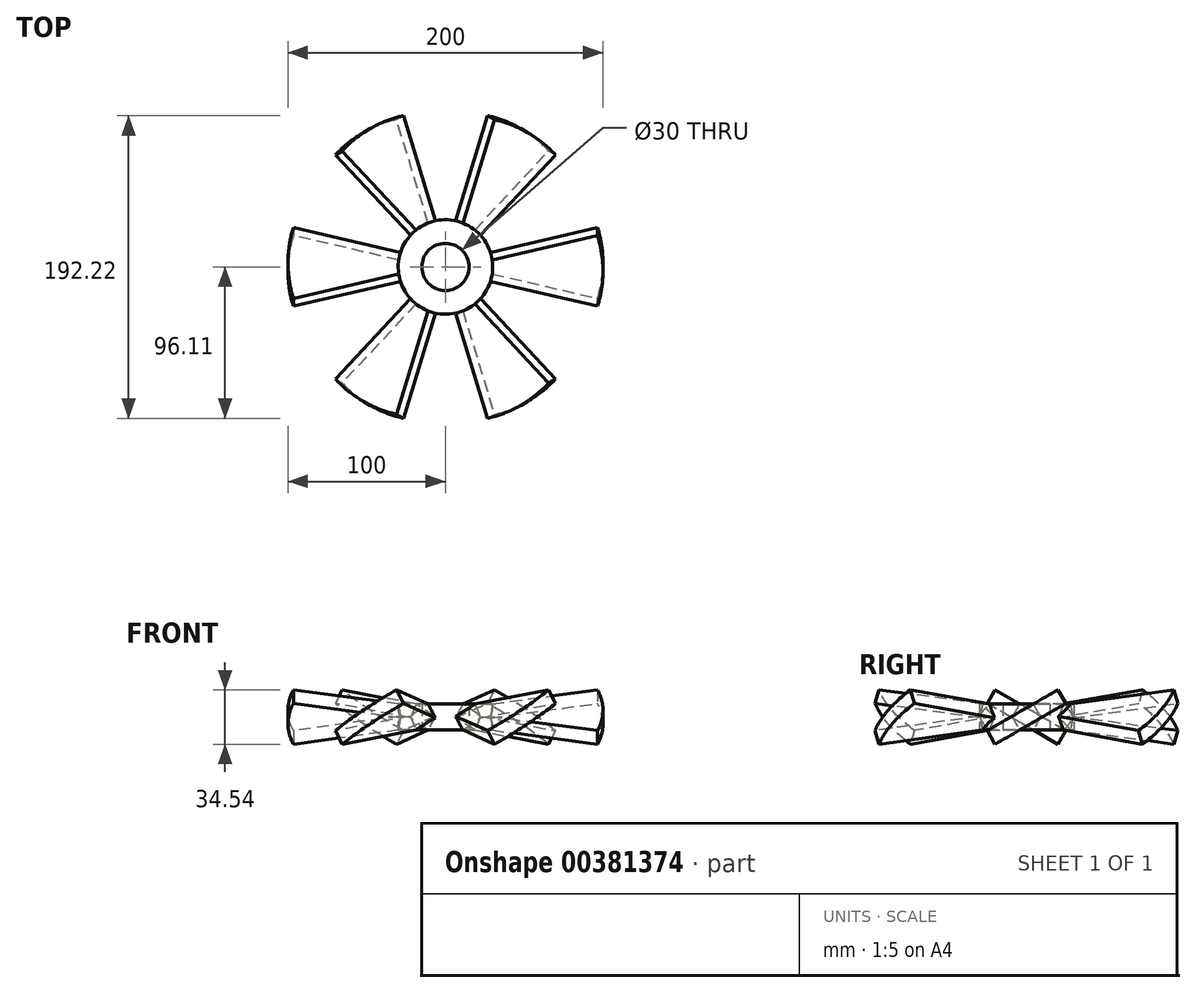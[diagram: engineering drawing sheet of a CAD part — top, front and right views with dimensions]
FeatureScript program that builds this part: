
annotation { "Feature Type Name" : "Feature", "Feature Type Description" : "" }
export const myFeature = defineFeature(function(context is Context, id is Id, definition is map)
    precondition{}
    {
        {
            var Q0;
            Q0=qCreatedBy(makeId("Top.planeOp"),FACE);
            var sketch = newSketch(context, id + "F0", { "sketchPlane" : qUnion([Q0])});
            skLineSegment(sketch, "E0", {"start": v(0, 0) * mm, "end": v(96.6, -25.88) * mm});
            skArc(sketch, "E1", {"start": v(96.6, -25.88) * mm, "mid": v(100, 0) * mm, "end": v(96.6, 25.88) * mm});
            skLineSegment(sketch, "E2", {"start": v(0, 0) * mm, "end": v(125.13, 0) * mm, "construction": true});
            skPoint(sketch, "E2.endSnap0", {"position": v(100, 0) * mm});
            skLineSegment(sketch, "E3.MirrorCS", {"start": v(0, 0) * mm, "end": v(96.6, 25.88) * mm});
            skSolve(sketch);
        }
        {
            var Q0;
            Q0=makeQuery(id+"F0.imprint","IMPRINT",FACE,{"disambiguationData":[TD([[makeQuery(id+"F0.imprint","IMPRINT",EDGE,{"derivedFrom":sQuery(id+"F0.wireOp",EDGE,"E0")}),1.0]])]});
            extrude(context, id + "F1", {"entities" : qUnion([Q0]), "depth" : 5 * mm, "hasSecondDirection" : true, "secondDirectionOppositeDirection" : true, "secondDirectionDepth" : 5 * mm});
        }
        {
            var Q0;
            Q0=qCreatedBy(makeId("Top.planeOp"),FACE);
            var sketch = newSketch(context, id + "F2", { "sketchPlane" : qUnion([Q0])});
            skLineSegment(sketch, "E4", {"start": v(0, 0) * mm, "end": v(131.6, 0) * mm, "construction": true});
            skSolve(sketch);
        }
        {
            var Q0;
            Q0=makeQuery(id+"F1.opExtrude","SWEPT_BODY",BODY,{"disambiguationData":[OSD([sQuery(id+"F0.wireOp",EDGE,"E0"),sQuery(id+"F0.wireOp",EDGE,"E1"),sQuery(id+"F0.wireOp",EDGE,"E3.MirrorCS")])]});
            var Q1;
            Q1=sQuery(id+"F2.wireOp",EDGE,"E4");
            transform(context, id + "F3", {"entities" : qUnion([Q0]), "transformType" : TransformType.ROTATION, "transformAxis" : qUnion([Q1]), "angle" : 30 * degree, "makeCopy" : false});
        }
        {
            var Q0;
            Q0=qCreatedBy(makeId("Right.planeOp"),FACE);
            var sketch = newSketch(context, id + "F4", { "sketchPlane" : qUnion([Q0])});
            skLineSegment(sketch, "E5", {"start": v(0, 0) * mm, "end": v(0, 57.62) * mm, "construction": true});
            skSolve(sketch);
        }
        {
            var Q0;
            Q0=makeQuery(id+"F1.opExtrude","SWEPT_BODY",BODY,{"disambiguationData":[OSD([sQuery(id+"F0.wireOp",EDGE,"E0"),sQuery(id+"F0.wireOp",EDGE,"E1"),sQuery(id+"F0.wireOp",EDGE,"E3.MirrorCS")])]});
            var Q1;
            Q1=sQuery(id+"F4.wireOp",EDGE,"E5");
            circularPattern(context, id + "F5", {"entities" : qUnion([Q0]), "axis" : qUnion([Q1]), "angle" : 360 * degree, "instanceCount" : 6, "equalSpace" : true});
        }
        {
            var Q0;
            Q0=qCreatedBy(makeId("Top.planeOp"),FACE);
            var sketch = newSketch(context, id + "F6", { "sketchPlane" : qUnion([Q0])});
            skCircle(sketch, "E6", {"center": v(0, 0) * mm, "radius": 30 * mm});
            skSolve(sketch);
        }
        {
            var Q0;
            Q0=makeQuery(id+"F6.imprint","IMPRINT",FACE,{"disambiguationData":[TD([[makeQuery(id+"F6.imprint","IMPRINT",EDGE,{"derivedFrom":sQuery(id+"F6.wireOp",EDGE,"E6")}),1.0]])]});
            var Q1;
            Q1=sQuery(id+"F6.wireOp",EDGE,"E6");
            extrude(context, id + "F7", {"entities" : qUnion([Q0]), "surfaceEntities" : qUnion([Q1]), "depth" : 25 * mm, "hasSecondDirection" : true, "secondDirectionOppositeDirection" : true, "secondDirectionDepth" : 25 * mm});
        }
        {
            var Q0;
            Q0=makeQuery(id+"F5.opPattern","COPY",BODY,{"derivedFrom":makeQuery(id+"F1.opExtrude","SWEPT_BODY",BODY,{"disambiguationData":[OSD([sQuery(id+"F0.wireOp",EDGE,"E0"),sQuery(id+"F0.wireOp",EDGE,"E1"),sQuery(id+"F0.wireOp",EDGE,"E3.MirrorCS")])]}),"instanceName":"3"});
            var Q1;
            Q1=makeQuery(id+"F5.opPattern","COPY",BODY,{"derivedFrom":makeQuery(id+"F1.opExtrude","SWEPT_BODY",BODY,{"disambiguationData":[OSD([sQuery(id+"F0.wireOp",EDGE,"E0"),sQuery(id+"F0.wireOp",EDGE,"E1"),sQuery(id+"F0.wireOp",EDGE,"E3.MirrorCS")])]}),"instanceName":"4"});
            var Q2;
            Q2=makeQuery(id+"F1.opExtrude","SWEPT_BODY",BODY,{"disambiguationData":[OSD([sQuery(id+"F0.wireOp",EDGE,"E0"),sQuery(id+"F0.wireOp",EDGE,"E1"),sQuery(id+"F0.wireOp",EDGE,"E3.MirrorCS")])]});
            var Q3;
            Q3=makeQuery(id+"F5.opPattern","COPY",BODY,{"derivedFrom":makeQuery(id+"F1.opExtrude","SWEPT_BODY",BODY,{"disambiguationData":[OSD([sQuery(id+"F0.wireOp",EDGE,"E0"),sQuery(id+"F0.wireOp",EDGE,"E1"),sQuery(id+"F0.wireOp",EDGE,"E3.MirrorCS")])]}),"instanceName":"1"});
            var Q4;
            Q4=makeQuery(id+"F5.opPattern","COPY",BODY,{"derivedFrom":makeQuery(id+"F1.opExtrude","SWEPT_BODY",BODY,{"disambiguationData":[OSD([sQuery(id+"F0.wireOp",EDGE,"E0"),sQuery(id+"F0.wireOp",EDGE,"E1"),sQuery(id+"F0.wireOp",EDGE,"E3.MirrorCS")])]}),"instanceName":"2"});
            var Q5;
            Q5=makeQuery(id+"F5.opPattern","COPY",BODY,{"derivedFrom":makeQuery(id+"F1.opExtrude","SWEPT_BODY",BODY,{"disambiguationData":[OSD([sQuery(id+"F0.wireOp",EDGE,"E0"),sQuery(id+"F0.wireOp",EDGE,"E1"),sQuery(id+"F0.wireOp",EDGE,"E3.MirrorCS")])]}),"instanceName":"5"});
            var Q6;
            Q6=makeQuery(id+"F7.opExtrude","SWEPT_BODY",BODY,{"disambiguationData":[OSD([sQuery(id+"F6.wireOp",EDGE,"E6")])]});
            booleanBodies(context, id + "F8", {"operationType" : BooleanOperationType.UNION, "tools" : qUnion([Q0, Q1, Q2, Q3, Q4, Q5, Q6])});
        }
        {
            var Q0;
            {var subQ0=sQuery(id+"F0.wireOp",EDGE,"E3.MirrorCS");Q0=makeQuery(id+"F8.opBoolean","INTERSECT",VERTEX,{"derivedFrom":[makeQuery(id+"F5.opPattern","COPY",FACE,{"derivedFrom":makeQuery(id+"F1.opExtrude","CAP_FACE",FACE,{"disambiguationData":[OSD([sQuery(id+"F0.wireOp",EDGE,"E0"),sQuery(id+"F0.wireOp",EDGE,"E1"),subQ0])],"isStart":false}),"instanceName":"4"}),makeQuery(id+"F5.opPattern","COPY",FACE,{"derivedFrom":makeQuery(id+"F1.opExtrude","SWEPT_FACE",FACE,{"disambiguationData":[OSD([subQ0])]}),"instanceName":"4"}),makeQuery(id+"F7.opExtrude","SWEPT_FACE",FACE,{"disambiguationData":[OSD([sQuery(id+"F6.wireOp",EDGE,"E6")])]})]});}
            var Q1;
            {var subQ0=sQuery(id+"F0.wireOp",EDGE,"E3.MirrorCS");Q1=makeQuery(id+"F8.opBoolean","INTERSECT",VERTEX,{"derivedFrom":[makeQuery(id+"F1.opExtrude","CAP_FACE",FACE,{"disambiguationData":[OSD([sQuery(id+"F0.wireOp",EDGE,"E0"),sQuery(id+"F0.wireOp",EDGE,"E1"),subQ0])],"isStart":false}),makeQuery(id+"F1.opExtrude","SWEPT_FACE",FACE,{"disambiguationData":[OSD([subQ0])]}),makeQuery(id+"F7.opExtrude","SWEPT_FACE",FACE,{"disambiguationData":[OSD([sQuery(id+"F6.wireOp",EDGE,"E6")])]})]});}
            var Q2;
            {var subQ0=sQuery(id+"F0.wireOp",EDGE,"E3.MirrorCS");Q2=makeQuery(id+"F8.opBoolean","INTERSECT",VERTEX,{"derivedFrom":[makeQuery(id+"F5.opPattern","COPY",FACE,{"derivedFrom":makeQuery(id+"F1.opExtrude","CAP_FACE",FACE,{"disambiguationData":[OSD([sQuery(id+"F0.wireOp",EDGE,"E0"),sQuery(id+"F0.wireOp",EDGE,"E1"),subQ0])],"isStart":false}),"instanceName":"2"}),makeQuery(id+"F5.opPattern","COPY",FACE,{"derivedFrom":makeQuery(id+"F1.opExtrude","SWEPT_FACE",FACE,{"disambiguationData":[OSD([subQ0])]}),"instanceName":"2"}),makeQuery(id+"F7.opExtrude","SWEPT_FACE",FACE,{"disambiguationData":[OSD([sQuery(id+"F6.wireOp",EDGE,"E6")])]})]});}
            cPlane(context, id + "F9", {"entities" : qUnion([Q0, Q1, Q2]), "cplaneType" : CPlaneType.THREE_POINT, "offset" : 25 * mm, "width" : 150 * mm, "height" : 150 * mm});
        }
        {
            var Q0;
            Q0=makeQuery(id+"F7.opExtrude","CAP_FACE",FACE,{"disambiguationData":[OSD([sQuery(id+"F6.wireOp",EDGE,"E6")])],"isStart":false});
            var Q1;
            Q1=qCreatedBy(id+"F9.planeOp",FACE);
            extrude(context, id + "F10", {"entities" : qUnion([Q0]), "operationType" : NewBodyOperationType.REMOVE, "endBound" : BoundingType.UP_TO_SURFACE, "oppositeDirection" : true, "endBoundEntityFace" : qUnion([Q1]), "depth" : 25 * mm});
        }
        {
            var Q0;
            {var subQ0=sQuery(id+"F0.wireOp",EDGE,"E0");Q0=makeQuery(id+"F8.opBoolean","INTERSECT",VERTEX,{"derivedFrom":[makeQuery(id+"F5.opPattern","COPY",FACE,{"derivedFrom":makeQuery(id+"F1.opExtrude","SWEPT_FACE",FACE,{"disambiguationData":[OSD([subQ0])]}),"instanceName":"2"}),makeQuery(id+"F5.opPattern","COPY",FACE,{"derivedFrom":makeQuery(id+"F1.opExtrude","CAP_FACE",FACE,{"disambiguationData":[OSD([subQ0,sQuery(id+"F0.wireOp",EDGE,"E1"),sQuery(id+"F0.wireOp",EDGE,"E3.MirrorCS")])],"isStart":true}),"instanceName":"2"}),makeQuery(id+"F7.opExtrude","SWEPT_FACE",FACE,{"disambiguationData":[OSD([sQuery(id+"F6.wireOp",EDGE,"E6")])]})]});}
            var Q1;
            {var subQ0=sQuery(id+"F0.wireOp",EDGE,"E0");Q1=makeQuery(id+"F8.opBoolean","INTERSECT",VERTEX,{"derivedFrom":[makeQuery(id+"F1.opExtrude","SWEPT_FACE",FACE,{"disambiguationData":[OSD([subQ0])]}),makeQuery(id+"F1.opExtrude","CAP_FACE",FACE,{"disambiguationData":[OSD([subQ0,sQuery(id+"F0.wireOp",EDGE,"E1"),sQuery(id+"F0.wireOp",EDGE,"E3.MirrorCS")])],"isStart":true}),makeQuery(id+"F7.opExtrude","SWEPT_FACE",FACE,{"disambiguationData":[OSD([sQuery(id+"F6.wireOp",EDGE,"E6")])]})]});}
            var Q2;
            {var subQ0=sQuery(id+"F0.wireOp",EDGE,"E0");Q2=makeQuery(id+"F8.opBoolean","INTERSECT",VERTEX,{"derivedFrom":[makeQuery(id+"F5.opPattern","COPY",FACE,{"derivedFrom":makeQuery(id+"F1.opExtrude","SWEPT_FACE",FACE,{"disambiguationData":[OSD([subQ0])]}),"instanceName":"4"}),makeQuery(id+"F5.opPattern","COPY",FACE,{"derivedFrom":makeQuery(id+"F1.opExtrude","CAP_FACE",FACE,{"disambiguationData":[OSD([subQ0,sQuery(id+"F0.wireOp",EDGE,"E1"),sQuery(id+"F0.wireOp",EDGE,"E3.MirrorCS")])],"isStart":true}),"instanceName":"4"}),makeQuery(id+"F7.opExtrude","SWEPT_FACE",FACE,{"disambiguationData":[OSD([sQuery(id+"F6.wireOp",EDGE,"E6")])]})]});}
            cPlane(context, id + "F11", {"entities" : qUnion([Q0, Q1, Q2]), "cplaneType" : CPlaneType.THREE_POINT, "offset" : 25 * mm, "width" : 150 * mm, "height" : 150 * mm});
        }
        {
            var Q0;
            Q0=makeQuery(id+"F7.opExtrude","CAP_FACE",FACE,{"disambiguationData":[OSD([sQuery(id+"F6.wireOp",EDGE,"E6")])],"isStart":true});
            var Q1;
            Q1=qCreatedBy(id+"F11.planeOp",FACE);
            extrude(context, id + "F12", {"entities" : qUnion([Q0]), "operationType" : NewBodyOperationType.REMOVE, "endBound" : BoundingType.UP_TO_SURFACE, "oppositeDirection" : true, "endBoundEntityFace" : qUnion([Q1]), "depth" : 25 * mm});
        }
        {
            var Q0;
            Q0=makeQuery(id+"F12.boolean.opBoolean","COPY",FACE,{"derivedFrom":makeQuery(id+"F12.opExtrude","CAP_FACE",FACE,{"disambiguationData":[OSD([sQuery(id+"F6.wireOp",EDGE,"E6")])],"isStart":false})});
            var sketch = newSketch(context, id + "F13", { "sketchPlane" : qUnion([Q0])});
            skCircle(sketch, "E7", {"center": v(0, 0) * mm, "radius": 15 * mm});
            skSolve(sketch);
        }
        {
            var Q0;
            Q0=makeQuery(id+"F13.imprint","IMPRINT",FACE,{"disambiguationData":[TD([[makeQuery(id+"F13.imprint","IMPRINT",EDGE,{"derivedFrom":sQuery(id+"F13.wireOp",EDGE,"E7")}),1.0]])]});
            extrude(context, id + "F14", {"entities" : qUnion([Q0]), "operationType" : NewBodyOperationType.REMOVE, "endBound" : BoundingType.UP_TO_NEXT, "oppositeDirection" : true, "depth" : 25 * mm});
        }
    });
